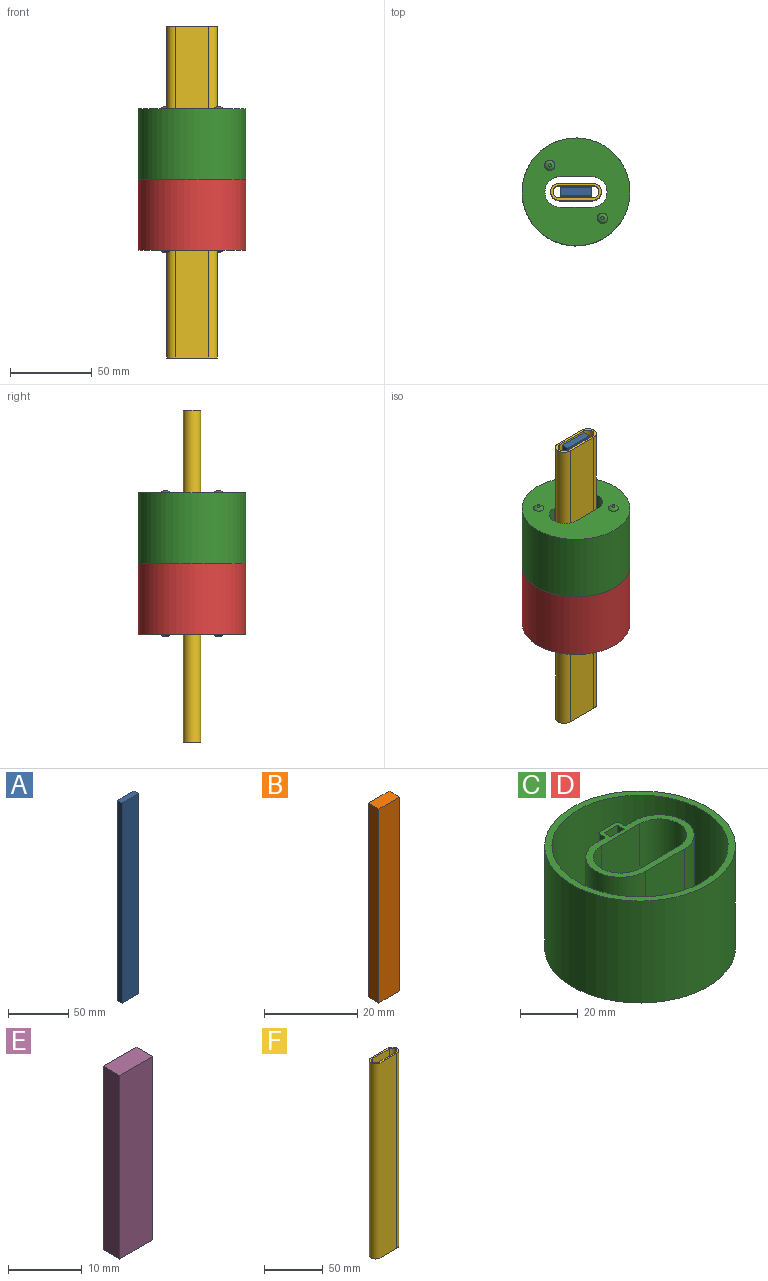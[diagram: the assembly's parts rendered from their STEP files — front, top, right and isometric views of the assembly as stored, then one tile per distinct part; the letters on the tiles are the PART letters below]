
ASSEMBLY  parts=6 mates=4
PART A: 6 faces, bbox 19.1x5.1x203.2 mm
  f0: plane 203.2x19.05mm, normal (0,-1,0), area 3871mm2, adj f1,f3,f4,f5
  f1: plane 203.2x5.08mm, normal (1,0,0), area 1032.3mm2, adj f0,f2,f4,f5
  f2: plane 203.2x19.05mm, normal (0,1,0), area 3871mm2, adj f1,f3,f4,f5
  f3: plane 203.2x5.08mm, normal (-1,0,0), area 1032.3mm2, adj f0,f2,f4,f5
  f4: plane 19.05x5.08mm, normal (0,0,1), area 96.8mm2, adj f0,f1,f2,f3
  f5: plane 19.05x5.08mm, normal (0,0,-1), area 96.8mm2, adj f0,f1,f2,f3
PART B: 6 faces, bbox 6.4x3.2x50.8 mm
  f0: plane 50.8x6.35mm, normal (0,-1,0), area 322.6mm2, adj f1,f3,f4,f5
  f1: plane 50.8x3.18mm, normal (1,0,0), area 161.3mm2, adj f0,f2,f4,f5
  f2: plane 50.8x6.35mm, normal (0,1,0), area 322.6mm2, adj f1,f3,f4,f5
  f3: plane 50.8x3.18mm, normal (-1,0,0), area 161.3mm2, adj f0,f2,f4,f5
  f4: plane 6.35x3.18mm, normal (0,0,1), area 20.2mm2, adj f0,f1,f2,f3
  f5: plane 6.35x3.18mm, normal (0,0,-1), area 20.2mm2, adj f0,f1,f2,f3
PART C: 31 faces, bbox 66x66x44.5 mm
  f0: plane 60.96x60.96mm, normal (0,0,1), area 1967.4mm2, adj f7,f12,f13,f14,f15,f16,f17,f18
  f1: plane 43.18x18.94mm, normal (0,-1,0), area 818mm2, adj f2,f5,f6,f25
  f2: cylinder r=9.53mm len=43.18mm, axis (0,0,-1), area 1293.5mm2, adj f1,f3,f6,f25
  f3: plane 43.18x18.94mm, normal (0,1,0), area 818mm2, adj f2,f5,f6,f25
  f4: cylinder r=33.02mm len=66.04mm, axis (0,0,-1), area 8958.6mm2, adj f6,f8
  f5: cylinder r=9.53mm len=43.18mm, axis (0,0,-1), area 1290.7mm2, adj f1,f3,f6,f25
  f6: plane 66.04x66.04mm, normal (0,0,-1), area 2716.1mm2, adj f1,f2,f3,f4,f5,f29,f30
  f7: cylinder r=30.48mm len=60.96mm, axis (0,0,-1), area 7783mm2, adj f0,f8
  f8: plane 66.04x66.04mm, normal (0,0,1), area 506.7mm2, adj f4,f7
  f9: plane 40.64x6.6mm, normal (0,-1,0), area 268.4mm2, adj f10,f24,f25,f26
  f10: plane 40.64x3.3mm, normal (-1,0,0), area 134.2mm2, adj f9,f11,f25,f26
  f11: plane 40.64x6.6mm, normal (0,1,0), area 268.4mm2, adj f10,f24,f25,f26
  f12: plane 40.64x8.13mm, normal (0,1,0), area 330.3mm2, adj f0,f13,f23,f25
  f13: cylinder r=0.76mm len=40.64mm, axis (0,0,-1), area 48.6mm2, adj f0,f12,f14,f25
  f14: plane 40.64x2.29mm, normal (-1,0,0), area 92.9mm2, adj f0,f13,f15,f25
  f15: cylinder r=0.76mm len=40.64mm, axis (0,0,-1), area 48.6mm2, adj f0,f14,f16,f25
  f16: plane 40.64x3.88mm, normal (0,1,0), area 157.9mm2, adj f0,f15,f17,f25
  f17: cylinder r=12.07mm len=40.64mm, axis (0,0,-1), area 1538.9mm2, adj f0,f16,f18,f25
  f18: plane 40.64x19.02mm, normal (0,-1,0), area 772.9mm2, adj f0,f17,f19,f25
  f19: cylinder r=12.07mm len=40.64mm, axis (0,0,-1), area 1538.9mm2, adj f0,f18,f20,f25
  f20: plane 40.64x3.88mm, normal (0,1,0), area 157.9mm2, adj f0,f19,f21,f25
  f21: cylinder r=0.76mm len=40.64mm, axis (0,0,-1), area 48.6mm2, adj f0,f20,f22,f25
  f22: plane 40.64x2.29mm, normal (1,0,0), area 92.9mm2, adj f0,f21,f23,f25
  f23: cylinder r=0.76mm len=40.64mm, axis (0,0,-1), area 48.6mm2, adj f0,f12,f22,f25
  f24: plane 40.64x3.3mm, normal (1,0,0), area 134.2mm2, adj f9,f11,f25,f26
  f25: plane 43.07x27.94mm, normal (0,0,1), area 283.5mm2, adj f1,f2,f3,f5,f9,f10,f11,f12
  f26: plane 6.6x3.3mm, normal (0,0,1), area 21.8mm2, adj f9,f10,f11,f24
  f27: plane 1.95x1.95mm, normal (0,0,-1), area 3mm2, adj f30
  f28: plane 1.95x1.95mm, normal (0,0,-1), area 3mm2, adj f29
  f29: torus R=0.98mm, axis (0,0,-1), area 36.6mm2, adj f6,f28
  f30: torus R=0.98mm, axis (0,0,-1), area 36.6mm2, adj f6,f27
PART D: same geometry as C
PART E: 6 faces, bbox 6.4x3.2x30.5 mm
  f0: plane 30.48x6.35mm, normal (0,-1,0), area 193.5mm2, adj f1,f3,f4,f5
  f1: plane 30.48x3.18mm, normal (1,0,0), area 96.8mm2, adj f0,f2,f4,f5
  f2: plane 30.48x6.35mm, normal (0,1,0), area 193.5mm2, adj f1,f3,f4,f5
  f3: plane 30.48x3.18mm, normal (-1,0,0), area 96.8mm2, adj f0,f2,f4,f5
  f4: plane 6.35x3.18mm, normal (0,0,1), area 20.2mm2, adj f0,f1,f2,f3
  f5: plane 6.35x3.18mm, normal (0,0,-1), area 20.2mm2, adj f0,f1,f2,f3
PART F: 10 faces, bbox 31x10.7x203.2 mm
  f0: cylinder r=5.33mm len=203.2mm, axis (0,0,-1), area 3405.1mm2, adj f1,f7,f8,f9
  f1: plane 203.2x20.32mm, normal (0,1,0), area 4129mm2, adj f0,f2,f8,f9
  f2: cylinder r=5.33mm len=203.2mm, axis (0,0,-1), area 3405.1mm2, adj f1,f7,f8,f9
  f3: cylinder r=3.81mm len=203.2mm, axis (0,0,-1), area 2432.2mm2, adj f4,f6,f8,f9
  f4: plane 203.2x20.32mm, normal (0,-1,0), area 4129mm2, adj f3,f5,f8,f9
  f5: cylinder r=3.81mm len=203.2mm, axis (0,0,-1), area 2432.2mm2, adj f4,f6,f8,f9
  f6: plane 203.2x20.32mm, normal (0,1,0), area 4129mm2, adj f3,f5,f8,f9
  f7: plane 203.2x20.32mm, normal (0,-1,0), area 4129mm2, adj f0,f2,f8,f9
  f8: plane 30.99x10.67mm, normal (0,0,1), area 105.7mm2, adj f0,f1,f2,f3,f4,f5,f6,f7
  f9: plane 30.99x10.67mm, normal (0,0,-1), area 105.7mm2, adj f0,f1,f2,f3,f4,f5,f6,f7
PLACE A rot(axis=(0,1,0),0deg) t=(-47.47,-9.41,-56.02)mm
PLACE B t=(28.75,3.29,12.56)mm
PLACE C rot(axis=(0,1,0),180deg) t=(-47.48,-9.41,96.38)mm
PLACE D t=(-47.51,-9.41,10.02)mm
PLACE E t=(28.75,3.29,12.56)mm
PLACE F rot(axis=(0,1,0),0deg) t=(-47.47,-9.41,-56.02)mm
MATE fastened F.f8 <-> A.f4  axis (0,0,1) through (-47.47,-9.41,147.18)mm
MATE fastened D.f26 <-> B.f5  axis (0,0,1) through (-47.49,3.29,12.56)mm
MATE fastened A.f4 <-> C.f4  axis (0,0,1) through (-47.47,-9.41,147.18)mm
MATE fastened E.f5 <-> B.f4  axis (0,0,-1) through (-47.49,3.29,63.36)mm
